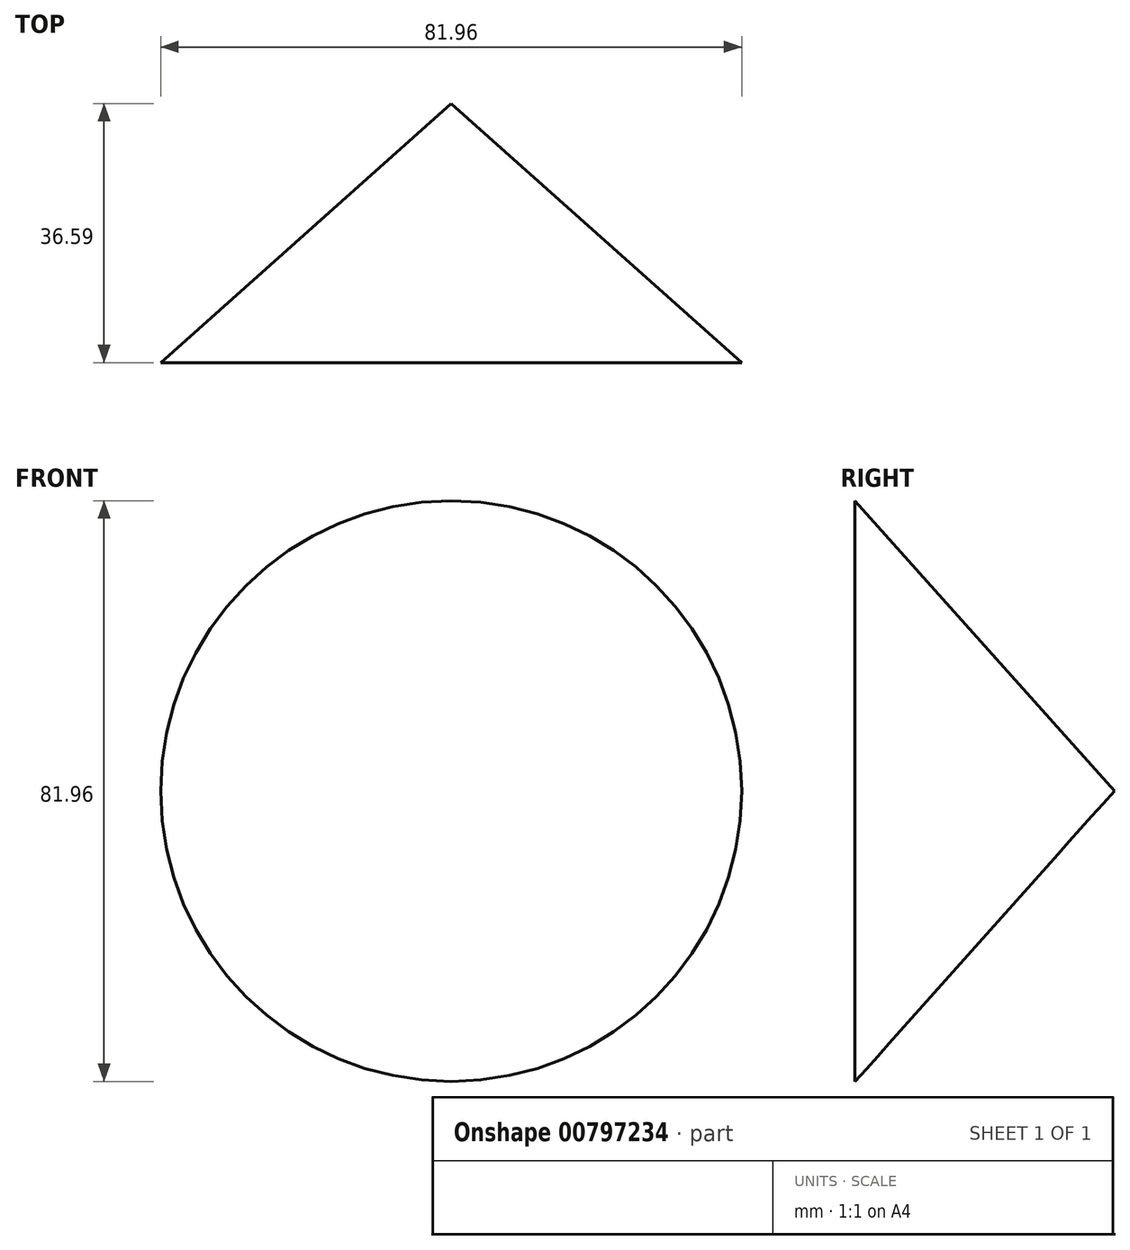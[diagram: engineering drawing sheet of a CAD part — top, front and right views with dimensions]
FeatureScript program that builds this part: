
annotation { "Feature Type Name" : "Feature", "Feature Type Description" : "" }
export const myFeature = defineFeature(function(context is Context, id is Id, definition is map)
    precondition{}
    {
        {
            var Q0;
            Q0=qCreatedBy(makeId("Top.planeOp"),FACE);
            var sketch = newSketch(context, id + "F0", { "sketchPlane" : qUnion([Q0])});
            skLineSegment(sketch, "E0", {"start": v(0, 0) * mm, "end": v(40.98, 36.59) * mm});
            skLineSegment(sketch, "E1", {"start": v(40.98, 36.59) * mm, "end": v(40.98, 0) * mm});
            skLineSegment(sketch, "E2", {"start": v(40.98, 0) * mm, "end": v(0, 0) * mm});
            skSolve(sketch);
        }
        {
            var Q0;
            Q0 = qSketchRegion(id + "F0", true);
            var Q1;
            Q1=sQuery(id+"F0.wireOp",EDGE,"E1");
            revolve(context, id + "F1", {"surfaceOperationType" : NewSurfaceOperationType.NEW, "entities" : qUnion([Q0]), "axis" : qUnion([Q1]), "revolveType" : RevolveType.FULL});
        }
    });
